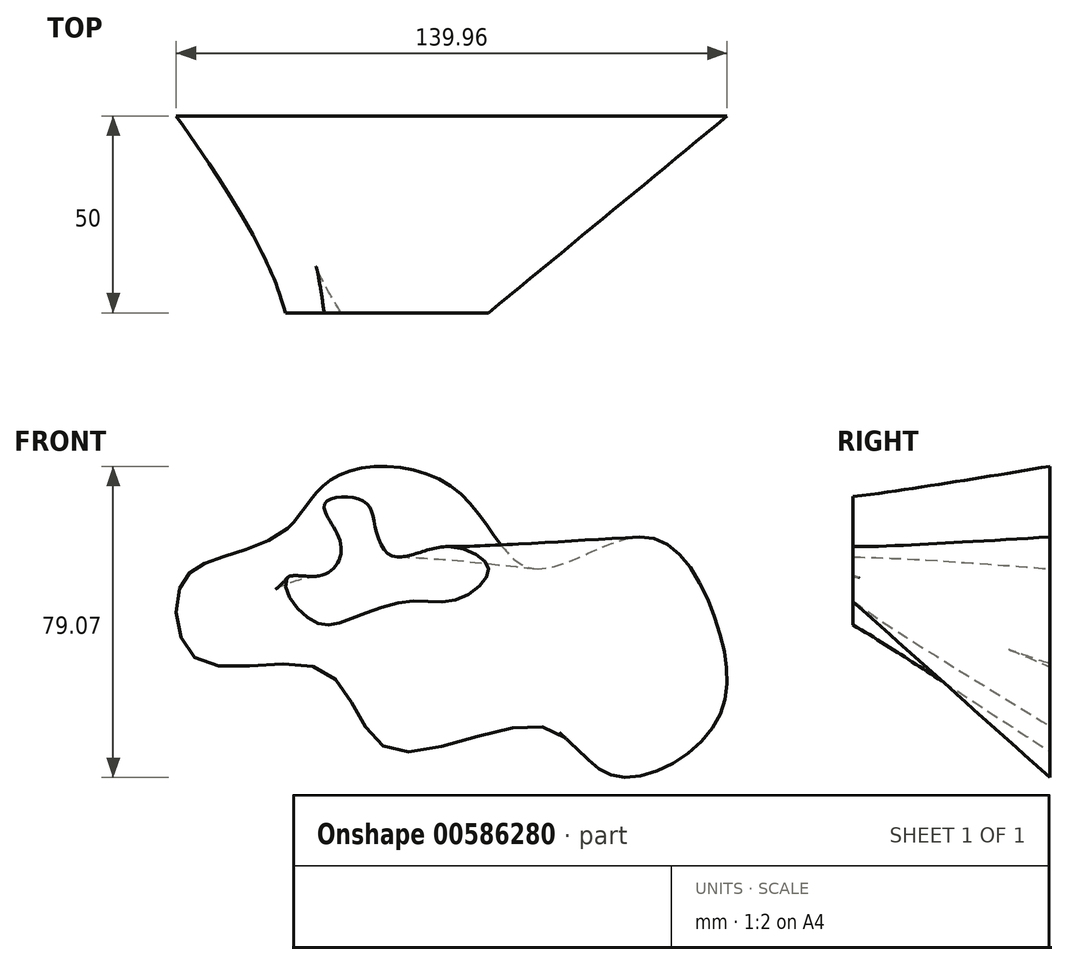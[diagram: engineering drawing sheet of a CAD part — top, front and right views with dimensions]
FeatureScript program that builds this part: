
annotation { "Feature Type Name" : "Feature", "Feature Type Description" : "" }
export const myFeature = defineFeature(function(context is Context, id is Id, definition is map)
    precondition{}
    {
        {
            var Q0;
            Q0=qCreatedBy(makeId("Front.planeOp"),FACE);
            var sketch = newSketch(context, id + "F0", { "sketchPlane" : qUnion([Q0])});
            skFitSpline(sketch, "E0", {"points": [v(-42.35, 30.1) * mm, v(-30.3, 43.1) * mm, v(0, 40.23) * mm, v(19.73, 19.95) * mm, v(48.82, 27.88) * mm, v(66.67, 6.06) * mm, v(65.57, -20.83) * mm, v(40.23, -32.73) * mm, v(22.37, -20.39) * mm, v(-16.64, -25.9) * mm, v(-32.95, -6.06) * mm, v(-64.91, -3.42) * mm, v(-69.54, 15.32) * mm, v(-60.06, 22.37) * mm, v(-42.35, 30.1) * mm]});
            skSolve(sketch);
        }
        {
            var Q0;
            Q0=qCreatedBy(makeId("Front.planeOp"),FACE);
            cPlane(context, id + "F1", {"entities" : qUnion([Q0]), "cplaneType" : CPlaneType.OFFSET, "offset" : 50 * mm, "width" : 152.4 * mm, "height" : 152.4 * mm});
        }
        {
            var Q0;
            Q0=qCreatedBy(id+"F1.planeOp",FACE);
            var sketch = newSketch(context, id + "F2", { "sketchPlane" : qUnion([Q0])});
            skFitSpline(sketch, "E1", {"points": [v(-33.01, 35.64) * mm, v(-28.75, 25.99) * mm, v(-33.49, 18.2) * mm, v(-42.23, 17.66) * mm, v(-41.55, 12.14) * mm, v(-34.12, 5.79) * mm, v(-26.5, 7) * mm, v(-11.44, 11.58) * mm, v(0.65, 11.92) * mm, v(8.45, 18.03) * mm, v(7.85, 21.58) * mm, v(-2.19, 25.43) * mm, v(-15.6, 23.02) * mm, v(-20, 30.17) * mm, v(-21.98, 36.16) * mm, v(-29.04, 38.08) * mm, v(-33.01, 35.64) * mm]});
            skSolve(sketch);
        }
        {
            var Q0;
            Q0=makeQuery(id+"F0.imprint","IMPRINT",FACE,{"disambiguationData":[TD([[makeQuery(id+"F0.imprint","IMPRINT",EDGE,{"derivedFrom":sQuery(id+"F0.wireOp",EDGE,"E0")}),-1.0]])]});
            var Q1;
            Q1=makeQuery(id+"F2.imprint","IMPRINT",FACE,{"disambiguationData":[TD([[makeQuery(id+"F2.imprint","IMPRINT",EDGE,{"derivedFrom":sQuery(id+"F2.wireOp",EDGE,"E1")}),1.0]])]});
            var Q2;
            Q2=sQuery(id+"F0.wireOp",EDGE,"E0");
            var Q3;
            Q3=sQuery(id+"F2.wireOp",EDGE,"E1");
            loft(context, id + "F3", {"sheetProfilesArray" : [{ "sheetProfileEntities" : qUnion([Q0]) }, { "sheetProfileEntities" : qUnion([Q1]) }], "wireProfilesArray" : [{ "wireProfileEntities" : qUnion([Q2]) }, { "wireProfileEntities" : qUnion([Q3]) }]});
        }
    });
